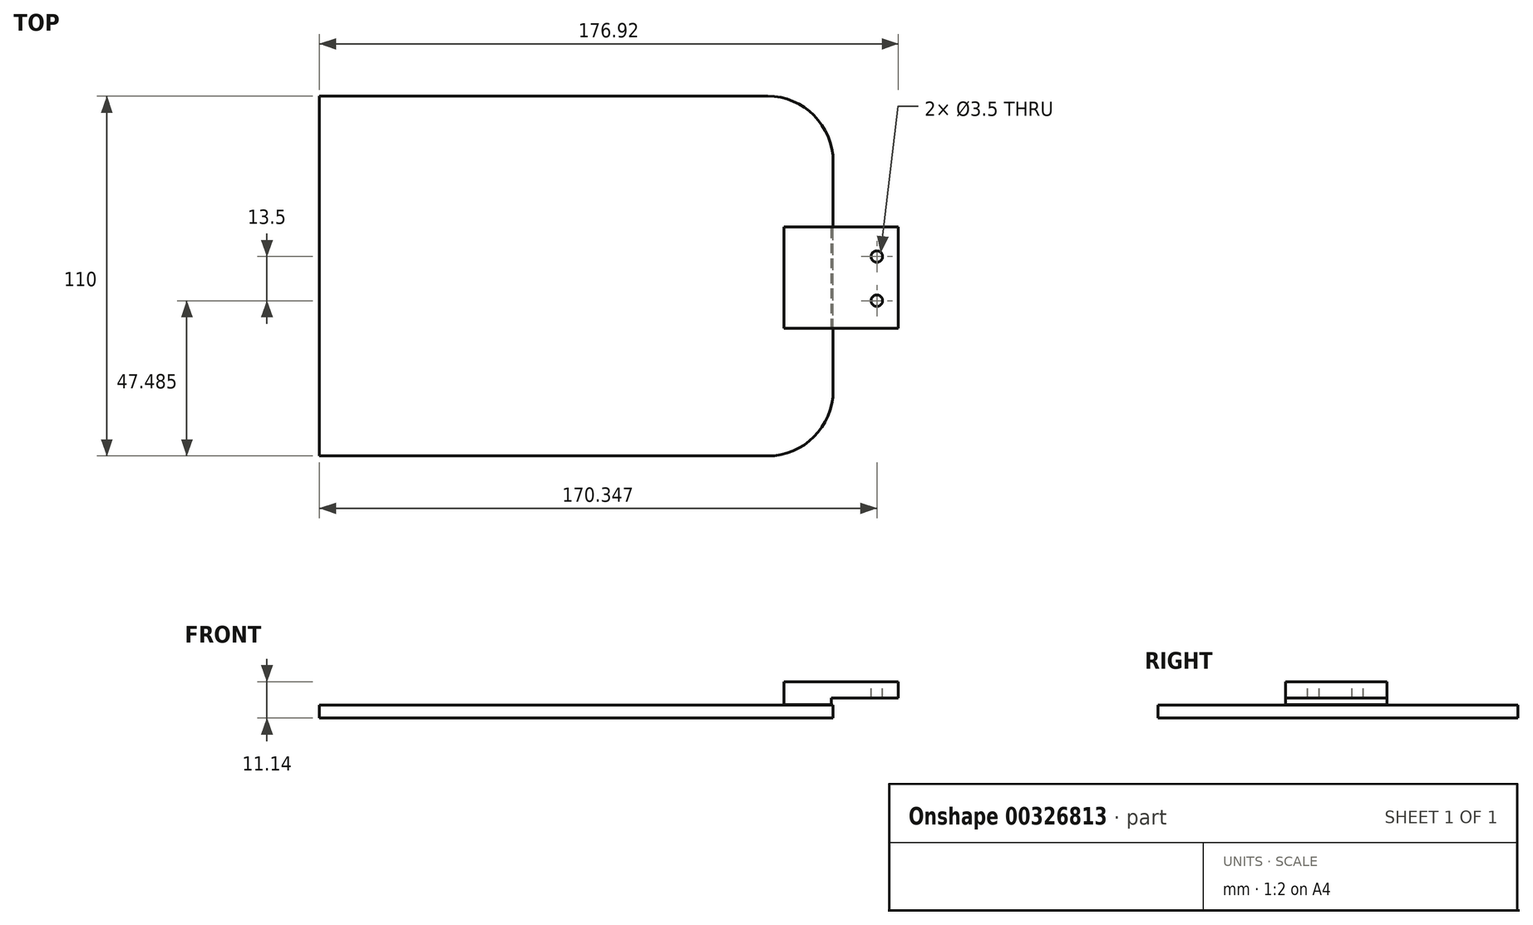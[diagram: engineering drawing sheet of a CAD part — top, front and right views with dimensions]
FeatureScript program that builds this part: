
annotation { "Feature Type Name" : "Feature", "Feature Type Description" : "" }
export const myFeature = defineFeature(function(context is Context, id is Id, definition is map)
    precondition{}
    {
        {
            var Q0;
            Q0=qCreatedBy(makeId("Front.planeOp"),FACE);
            var sketch = newSketch(context, id + "F0", { "sketchPlane" : qUnion([Q0])});
            skLineSegment(sketch, "E0.bottom", {"start": v(-78.5, 2) * mm, "end": v(78.5, 2) * mm});
            skLineSegment(sketch, "E0.top", {"start": v(-78.5, -2) * mm, "end": v(78.5, -2) * mm});
            skLineSegment(sketch, "E0.left", {"start": v(-78.5, 2) * mm, "end": v(-78.5, -2) * mm});
            skLineSegment(sketch, "E0.right", {"start": v(78.5, 2) * mm, "end": v(78.5, -2) * mm});
            skPoint(sketch, "E0.middle", {"position": v(0, 0) * mm});
            skSolve(sketch);
        }
        {
            var Q0;
            Q0=makeQuery(id+"F0.imprint","IMPRINT",FACE,{"disambiguationData":[TD([[makeQuery(id+"F0.imprint","IMPRINT",EDGE,{"derivedFrom":sQuery(id+"F0.wireOp",EDGE,"E0.bottom")}),-1.0]])]});
            extrude(context, id + "F1", {"entities" : qUnion([Q0]), "depth" : 110 * mm});
        }
        {
            var Q0;
            Q0=qCreatedBy(makeId("Front.planeOp"),FACE);
            var sketch = newSketch(context, id + "F2", { "sketchPlane" : qUnion([Q0])});
            skLineSegment(sketch, "E1", {"start": v(695.08, 8.84) * mm, "end": v(695.08, 16.84) * mm});
            skLineSegment(sketch, "E2", {"start": v(63.42, 2.14) * mm, "end": v(63.42, 9.14) * mm});
            skLineSegment(sketch, "E3", {"start": v(63.42, 9.14) * mm, "end": v(98.42, 9.14) * mm});
            skLineSegment(sketch, "E4", {"start": v(98.42, 9.14) * mm, "end": v(98.42, 4.14) * mm});
            skLineSegment(sketch, "E5", {"start": v(98.42, 4.14) * mm, "end": v(77.94, 4.14) * mm});
            skLineSegment(sketch, "E6", {"start": v(77.94, 4.14) * mm, "end": v(77.94, 2.14) * mm});
            skLineSegment(sketch, "E7", {"start": v(77.94, 2.14) * mm, "end": v(63.42, 2.14) * mm});
            skSolve(sketch);
        }
        {
            var Q0;
            Q0 = qSketchRegion(id + "F2", true);
            extrude(context, id + "F3", {"entities" : qUnion([Q0]), "depth" : 71 * mm});
        }
        {
            var Q0;
            Q0 = qSketchRegion(id + "F2", true);
            extrude(context, id + "F4", {"entities" : qUnion([Q0]), "operationType" : NewBodyOperationType.REMOVE, "depth" : 40 * mm});
        }
        {
            var Q0;
            Q0=makeQuery(id+"F1.opExtrude","CAP_EDGE",EDGE,{"disambiguationData":[OSD([sQuery(id+"F0.wireOp",EDGE,"E0.right")])],"isStart":false});
            fillet(context, id + "F5", {"entities" : qUnion([Q0]), "radius" : 20 * mm, "tangentPropagation" : true, "allowEdgeOverflow" : false});
        }
        {
            var Q0;
            Q0=makeQuery(id+"F1.opExtrude","CAP_EDGE",EDGE,{"disambiguationData":[OSD([sQuery(id+"F0.wireOp",EDGE,"E0.right")])],"isStart":true});
            fillet(context, id + "F6", {"entities" : qUnion([Q0]), "radius" : 20 * mm, "tangentPropagation" : true, "allowEdgeOverflow" : false});
        }
        {
            var Q0;
            Q0=qCreatedBy(makeId("Top.planeOp"),FACE);
            var sketch = newSketch(context, id + "F7", { "sketchPlane" : qUnion([Q0])});
            skCircle(sketch, "E8", {"center": v(91.85, -62.52) * mm, "radius": 1.75 * mm});
            skCircle(sketch, "E9", {"center": v(91.85, -49.02) * mm, "radius": 1.75 * mm});
            skSolve(sketch);
        }
        {
            var Q0;
            Q0 = qSketchRegion(id + "F7", true);
            extrude(context, id + "F8", {"entities" : qUnion([Q0]), "operationType" : NewBodyOperationType.ADD, "endBound" : BoundingType.SYMMETRIC, "depth" : 25 * mm, "offsetDistance" : 25 * mm});
        }
        {
            var Q0;
            Q0 = qSketchRegion(id + "F7", true);
            extrude(context, id + "F9", {"entities" : qUnion([Q0]), "operationType" : NewBodyOperationType.REMOVE, "endBound" : BoundingType.SYMMETRIC, "oppositeDirection" : true, "depth" : 25 * mm, "offsetDistance" : 25 * mm});
        }
    });
